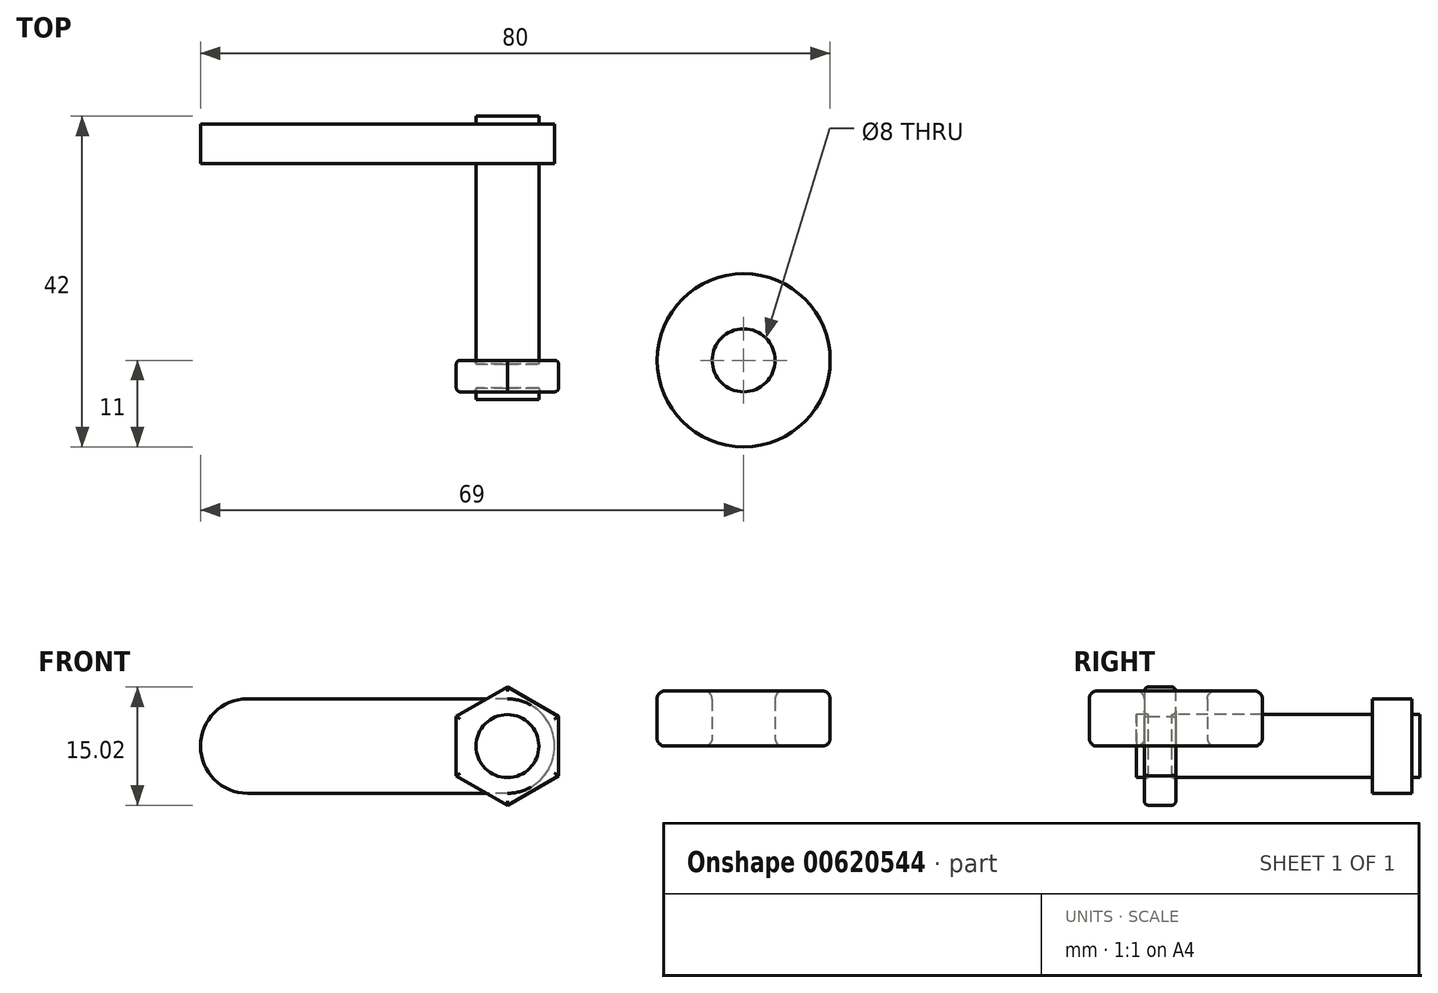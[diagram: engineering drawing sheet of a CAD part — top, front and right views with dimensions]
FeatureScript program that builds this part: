
annotation { "Feature Type Name" : "Feature", "Feature Type Description" : "" }
export const myFeature = defineFeature(function(context is Context, id is Id, definition is map)
    precondition{}
    {
        {
            var Q0;
            Q0=qCreatedBy(makeId("Top.planeOp"),FACE);
            var sketch = newSketch(context, id + "F0", { "sketchPlane" : qUnion([Q0])});
            skCircle(sketch, "E0", {"center": v(0, 0) * mm, "radius": 4 * mm});
            skCircle(sketch, "E1", {"center": v(0, 0) * mm, "radius": 11 * mm});
            skSolve(sketch);
        }
        {
            var Q0;
            Q0 = qSketchRegion(id + "F0", true);
            extrude(context, id + "F1", {"entities" : qUnion([Q0]), "depth" : 7 * mm, "offsetDistance" : 25 * mm});
        }
        {
            var Q0;
            Q0=makeQuery(id+"F1.opExtrude","CAP_EDGE",EDGE,{"disambiguationData":[OSD([sQuery(id+"F0.wireOp",EDGE,"E1")])],"isStart":false});
            var Q1;
            Q1=makeQuery(id+"F1.opExtrude","SWEPT_FACE",FACE,{"disambiguationData":[OSD([sQuery(id+"F0.wireOp",EDGE,"E1")])]});
            var Q2;
            Q2=makeQuery(id+"F1.opExtrude","CAP_EDGE",EDGE,{"disambiguationData":[OSD([sQuery(id+"F0.wireOp",EDGE,"E0")])],"isStart":false});
            var Q3;
            Q3=makeQuery(id+"F1.opExtrude","SWEPT_FACE",FACE,{"disambiguationData":[OSD([sQuery(id+"F0.wireOp",EDGE,"E0")])]});
            fillet(context, id + "F2", {"entities" : qUnion([Q0, Q1, Q2, Q3]), "radius" : 1 * mm, "tangentPropagation" : true, "allowEdgeOverflow" : false});
        }
        {
            var Q0;
            Q0=qCreatedBy(makeId("Front.planeOp"),FACE);
            var sketch = newSketch(context, id + "F3", { "sketchPlane" : qUnion([Q0])});
            skCircle(sketch, "E2.cCircle", {"center": v(-30, 0) * mm, "radius": 6.5 * mm, "construction": true});
            skLineSegment(sketch, "E2.0", {"start": v(-23.5, 3.75) * mm, "end": v(-23.5, -3.75) * mm});
            skLineSegment(sketch, "E2.1", {"start": v(-23.5, -3.75) * mm, "end": v(-30, -7.5) * mm});
            skLineSegment(sketch, "E2.2", {"start": v(-30, -7.5) * mm, "end": v(-36.5, -3.75) * mm});
            skLineSegment(sketch, "E2.3", {"start": v(-36.5, -3.75) * mm, "end": v(-36.5, 3.75) * mm});
            skLineSegment(sketch, "E2.4", {"start": v(-36.5, 3.75) * mm, "end": v(-30, 7.5) * mm});
            skLineSegment(sketch, "E2.5", {"start": v(-30, 7.5) * mm, "end": v(-23.5, 3.75) * mm});
            skPoint(sketch, "E2.0.midPoint", {"position": v(-23.5, 0) * mm});
            skCircle(sketch, "E3", {"center": v(-30, 0) * mm, "radius": 4 * mm});
            skSolve(sketch);
        }
        {
            var Q0;
            Q0 = qSketchRegion(id + "F3", true);
            extrude(context, id + "F4", {"entities" : qUnion([Q0]), "depth" : 4 * mm, "offsetDistance" : 25 * mm});
        }
        {
            var Q0;
            Q0=makeQuery(id+"F4.opExtrude","CAP_FACE",FACE,{"disambiguationData":[OSD([sQuery(id+"F3.wireOp",EDGE,"E2.0"),sQuery(id+"F3.wireOp",EDGE,"E2.1"),sQuery(id+"F3.wireOp",EDGE,"E2.2"),sQuery(id+"F3.wireOp",EDGE,"E2.3"),sQuery(id+"F3.wireOp",EDGE,"E2.4"),sQuery(id+"F3.wireOp",EDGE,"E2.5"),sQuery(id+"F3.wireOp",EDGE,"E3")])],"isStart":false});
            var Q1;
            Q1=makeQuery(id+"F4.opExtrude","CAP_FACE",FACE,{"disambiguationData":[OSD([sQuery(id+"F3.wireOp",EDGE,"E2.0"),sQuery(id+"F3.wireOp",EDGE,"E2.1"),sQuery(id+"F3.wireOp",EDGE,"E2.2"),sQuery(id+"F3.wireOp",EDGE,"E2.3"),sQuery(id+"F3.wireOp",EDGE,"E2.4"),sQuery(id+"F3.wireOp",EDGE,"E2.5"),sQuery(id+"F3.wireOp",EDGE,"E3")])],"isStart":true});
            fillet(context, id + "F5", {"entities" : qUnion([Q0, Q1]), "radius" : 0.5 * mm, "tangentPropagation" : true, "allowEdgeOverflow" : false});
        }
        {
            var Q0;
            Q0=makeQuery(id+"F4.opExtrude","CAP_FACE",FACE,{"disambiguationData":[OSD([sQuery(id+"F3.wireOp",EDGE,"E2.0"),sQuery(id+"F3.wireOp",EDGE,"E2.1"),sQuery(id+"F3.wireOp",EDGE,"E2.2"),sQuery(id+"F3.wireOp",EDGE,"E2.3"),sQuery(id+"F3.wireOp",EDGE,"E2.4"),sQuery(id+"F3.wireOp",EDGE,"E2.5"),sQuery(id+"F3.wireOp",EDGE,"E3")])],"isStart":true});
            var sketch = newSketch(context, id + "F6", { "sketchPlane" : qUnion([Q0])});
            skCircle(sketch, "E4.0", {"center": v(30, 0) * mm, "radius": 4 * mm});
            skSolve(sketch);
        }
        {
            var Q0;
            Q0 = qSketchRegion(id + "F6", true);
            extrude(context, id + "F7", {"entities" : qUnion([Q0]), "operationType" : NewBodyOperationType.ADD, "depth" : 25 * mm, "offsetDistance" : 25 * mm, "hasSecondDirection" : true, "secondDirectionOppositeDirection" : true, "secondDirectionDepth" : 5 * mm});
        }
        {
            var Q0;
            Q0=makeQuery(id+"F7.opExtrude","CAP_FACE",FACE,{"disambiguationData":[OSD([sQuery(id+"F6.wireOp",EDGE,"E4.0")])],"isStart":false});
            var sketch = newSketch(context, id + "F8", { "sketchPlane" : qUnion([Q0])});
            skCircle(sketch, "E5.0.0", {"center": v(30, 0) * mm, "radius": 4 * mm});
            skLineSegment(sketch, "E6.bottom", {"start": v(30, 6) * mm, "end": v(63, 6) * mm});
            skLineSegment(sketch, "E6.top", {"start": v(24, 0) * mm, "end": v(69, 0) * mm, "construction": true});
            skLineSegment(sketch, "E6.left", {"start": v(24, 0) * mm, "end": v(24, 0) * mm});
            skLineSegment(sketch, "E6.right", {"start": v(69, 0) * mm, "end": v(69, 0) * mm});
            skPoint(sketch, "E7.visualSharp", {"position": v(24, 6) * mm});
            skArc(sketch, "E7.filletArc", {"start": v(30, 6) * mm, "mid": v(25.76, 4.24) * mm, "end": v(24, 0) * mm});
            skPoint(sketch, "E8.visualSharp", {"position": v(69, 6) * mm});
            skArc(sketch, "E8.filletArc", {"start": v(69, 0) * mm, "mid": v(67.24, 4.24) * mm, "end": v(63, 6) * mm});
            skLineSegment(sketch, "E9.MirrorCS", {"start": v(30, -6) * mm, "end": v(63, -6) * mm});
            skArc(sketch, "E10.MirrorCS", {"start": v(30, -6) * mm, "mid": v(25.76, -4.24) * mm, "end": v(24, 0) * mm});
            skArc(sketch, "E11.MirrorCS", {"start": v(69, 0) * mm, "mid": v(67.24, -4.24) * mm, "end": v(63, -6) * mm});
            skSolve(sketch);
        }
        {
            var Q0;
            Q0 = qSketchRegion(id + "F8", true);
            extrude(context, id + "F9", {"entities" : qUnion([Q0]), "operationType" : NewBodyOperationType.ADD, "depth" : 5 * mm, "offsetDistance" : 25 * mm});
        }
        {
            var Q0;
            Q0=makeQuery(id+"F7.opExtrude","CAP_FACE",FACE,{"disambiguationData":[OSD([sQuery(id+"F6.wireOp",EDGE,"E4.0")])],"isStart":false});
            extrude(context, id + "F10", {"entities" : qUnion([Q0]), "operationType" : NewBodyOperationType.ADD, "depth" : 6 * mm, "offsetDistance" : 25 * mm});
        }
    });
